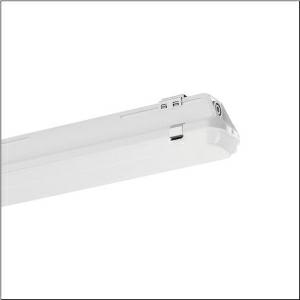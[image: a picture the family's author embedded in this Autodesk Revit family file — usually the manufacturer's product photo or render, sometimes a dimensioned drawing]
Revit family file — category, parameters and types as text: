
# Revit family: monsun_r__12_51fp107p430h_13b7
name_source: partatom
category: Lighting Fixtures
units: mm (PartAtom-declared; Revit-internal decimal feet)

## family parameters
Cut with Voids When Loaded = No
Host = Face
Light Source = No
Part Type = Normal
Room Calculation Point = No
Round Connector Dimension = Use Diameter
Shared = No

## types (1)
- Monsun® 12 (1 x LED, 3970 lm, 22.2 W, 4000K)
    Apparent Load = 22 VA
    CIE Flux Codes = 47 77 93 94 100
    Color Rendering = 80
    Color Temperature = 4000K
    Default Elevation = 1800 mm
    Description = Monsun® 12, damp-proof luminaire, chain hanger, primary optical cover: enclosure, of PMMA, light emission: direct distribution, primary light characteristic: symmetric, installation type: suspended mounting, surface-mounted, horizontal mounting, vertical mounting, LED rated luminous flux: 3.970 lm, light colour: 840, colour temperature: 4000K, control gear: ECG, with terminal, 3-pole, max. 2.5mm², mains connection: 220..240V, AC, 50/60Hz, rated input power: 22W, luminaire housing, of glass-fibre reinforced polyester, uncoated, bright grey, length: 1.590 mm, width: 90 mm, height: 88mm, clip for enclosure, of stainless steel (V2A), ceiling mounting element, of stainless steel (V2A), chain hanger, of stainless steel (V2A), protection rating (complete): IP66, insulation class (complete): insulation class I (protective earthing), certification: CE, ENEC, VDE, protection symbol: D, impact resistance: IK04, permissible ambient temperature for indoor applications: -35..+40°C, standard: EN 50419, EN 60598-2-1, no direct snow, no direct sun, no direct rain, for indoor or canopied outdoor use, corresponds to IFS (International Featured Standards) requirements for safety and quality in the food industry, for animal farming (ammonia tested): for use in cowhouse, pig house, horse-stables... (not for use in poultry stables), AT max for animal farming = 40°C, packaging unit: 1 piece
    Height = 89 mm
    Lamp = 1 x LED
    Lamp Light Flux = 3970 lm
    Lamp Power = 22.2 W
    Lamp count = 1
    Length = 1590 mm
    Luminous efficacy = 179 lm/W
    Manufacturer = Siteco
    ModVariant = No
    Model = 51FP107P430H
    Mounting Place = Ceiling
    Mounting Type = Pendant
    Number of Poles = 1
    OnlyDefault = Yes
    Power Factor = 1
    Product Name = Monsun® 12
    Product group = damp-proof luminaire | ceiling pendant
    ProductGroupID = 908
    Protection Class = Protection class I
    Protection Degree = IP 66
    RLX_Detail_Level = 1
    RlxData = <blob elided: 88589 chars, md5=96980bd4>
    Socket = socket
    Standby Power = 0 W
    System Light Flux = 3970 lm
    System Power = 22 W
    Type Comments = Product without accessories
    Type Image = l_1004748.jpg
    URL = http://relux.com
    VarID = ---
    Voltage = 0 V
    Weight = 0.00 kg
    Width = 90 mm

## geometry (parser evidence)
native form markers: Blend x4, Sweep x12
no freeform markers — native parametric forms only
